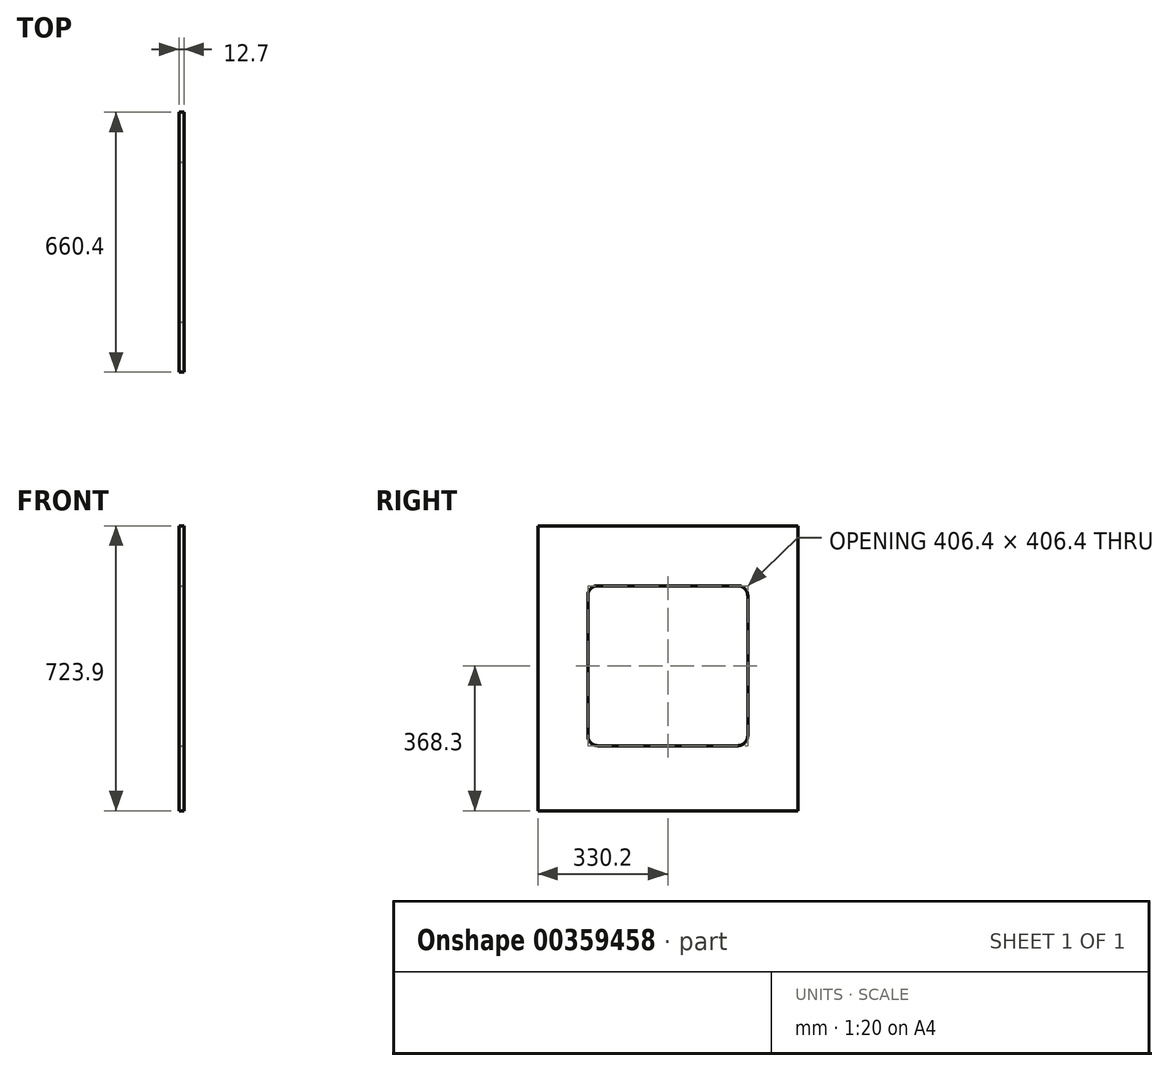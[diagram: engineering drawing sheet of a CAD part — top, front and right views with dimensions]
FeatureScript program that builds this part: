
annotation { "Feature Type Name" : "Feature", "Feature Type Description" : "" }
export const myFeature = defineFeature(function(context is Context, id is Id, definition is map)
    precondition{}
    {
        {
            var Q0;
            Q0=qCreatedBy(makeId("Right.planeOp"),FACE);
            var sketch = newSketch(context, id + "F0", { "sketchPlane" : qUnion([Q0])});
            skLineSegment(sketch, "E0.bottom", {"start": v(0, 0) * mm, "end": v(660.4, 0) * mm});
            skLineSegment(sketch, "E0.top", {"start": v(0, 723.9) * mm, "end": v(660.4, 723.9) * mm});
            skLineSegment(sketch, "E0.left", {"start": v(0, 0) * mm, "end": v(0, 723.9) * mm});
            skLineSegment(sketch, "E0.right", {"start": v(660.4, 0) * mm, "end": v(660.4, 723.9) * mm});
            skSolve(sketch);
        }
        {
            var Q0;
            Q0=makeQuery(id+"F0.imprint","IMPRINT",FACE,{"disambiguationData":[TD([[makeQuery(id+"F0.imprint","IMPRINT",EDGE,{"derivedFrom":sQuery(id+"F0.wireOp",EDGE,"E0.bottom")}),1.0]])]});
            extrude(context, id + "F1", {"entities" : qUnion([Q0]), "depth" : 12.7 * mm});
        }
        {
            var Q0;
            Q0=makeQuery(id+"F1.opExtrude","CAP_FACE",FACE,{"disambiguationData":[OSD([sQuery(id+"F0.wireOp",EDGE,"E0.bottom"),sQuery(id+"F0.wireOp",EDGE,"E0.top"),sQuery(id+"F0.wireOp",EDGE,"E0.left"),sQuery(id+"F0.wireOp",EDGE,"E0.right")])],"isStart":false});
            var sketch = newSketch(context, id + "F2", { "sketchPlane" : qUnion([Q0])});
            skLineSegment(sketch, "E1.bottom", {"start": v(152.4, 571.5) * mm, "end": v(508, 571.5) * mm});
            skLineSegment(sketch, "E1.top", {"start": v(152.4, 165.1) * mm, "end": v(508, 165.1) * mm});
            skLineSegment(sketch, "E1.left", {"start": v(127, 546.1) * mm, "end": v(127, 190.5) * mm});
            skLineSegment(sketch, "E1.right", {"start": v(533.4, 546.1) * mm, "end": v(533.4, 190.5) * mm});
            skPoint(sketch, "E2.visualSharp", {"position": v(127, 571.5) * mm});
            skArc(sketch, "E2.filletArc", {"start": v(152.4, 571.5) * mm, "mid": v(134.44, 564.06) * mm, "end": v(127, 546.1) * mm});
            skPoint(sketch, "E3.visualSharp", {"position": v(533.4, 571.5) * mm});
            skArc(sketch, "E3.filletArc", {"start": v(533.4, 546.1) * mm, "mid": v(525.96, 564.06) * mm, "end": v(508, 571.5) * mm});
            skPoint(sketch, "E4.visualSharp", {"position": v(533.4, 165.1) * mm});
            skArc(sketch, "E4.filletArc", {"start": v(508, 165.1) * mm, "mid": v(525.96, 172.54) * mm, "end": v(533.4, 190.5) * mm});
            skPoint(sketch, "E5.visualSharp", {"position": v(127, 165.1) * mm});
            skArc(sketch, "E5.filletArc", {"start": v(127, 190.5) * mm, "mid": v(134.44, 172.54) * mm, "end": v(152.4, 165.1) * mm});
            skSolve(sketch);
        }
        {
            var Q0;
            Q0=makeQuery(id+"F2.imprint","IMPRINT",FACE,{"disambiguationData":[TD([[makeQuery(id+"F2.imprint","IMPRINT",EDGE,{"derivedFrom":sQuery(id+"F2.wireOp",EDGE,"E1.bottom")}),-1.0]])]});
            extrude(context, id + "F3", {"entities" : qUnion([Q0]), "operationType" : NewBodyOperationType.REMOVE, "endBound" : BoundingType.THROUGH_ALL, "oppositeDirection" : true, "depth" : 25.4 * mm});
        }
    });
